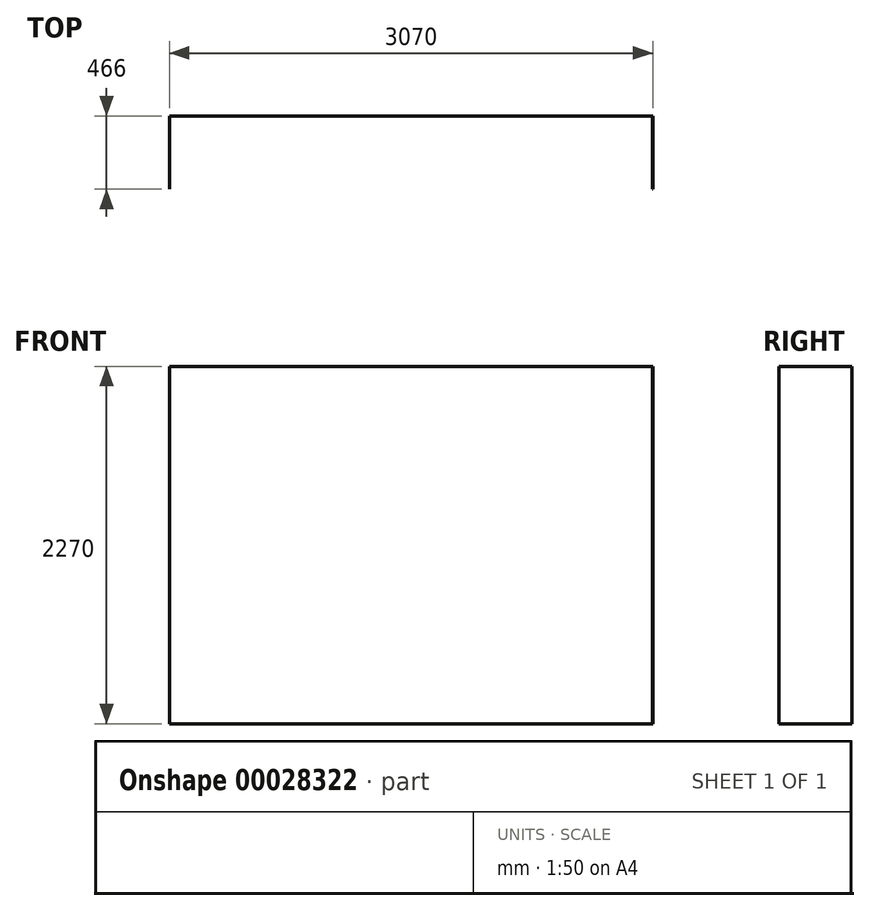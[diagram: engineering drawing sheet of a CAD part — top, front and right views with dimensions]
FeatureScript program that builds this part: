
annotation { "Feature Type Name" : "Feature", "Feature Type Description" : "" }
export const myFeature = defineFeature(function(context is Context, id is Id, definition is map)
    precondition{}
    {
        {
            var Q0;
            Q0=qCreatedBy(makeId("Front.planeOp"),FACE);
            var sketch = newSketch(context, id + "F0", { "sketchPlane" : qUnion([Q0])});
            skLineSegment(sketch, "E0.bottom", {"start": v(-1527.48, 1543.98) * mm, "end": v(1542.52, 1543.98) * mm});
            skLineSegment(sketch, "E0.top", {"start": v(-1527.48, -726.02) * mm, "end": v(1542.52, -726.02) * mm});
            skLineSegment(sketch, "E0.left", {"start": v(-1527.48, 1543.98) * mm, "end": v(-1527.48, -726.02) * mm});
            skLineSegment(sketch, "E0.right", {"start": v(1542.52, 1543.98) * mm, "end": v(1542.52, -726.02) * mm});
            skSolve(sketch);
        }
        {
            var Q0;
            Q0 = qSketchRegion(id + "F0", true);
            extrude(context, id + "F1", {"entities" : qUnion([Q0]), "oppositeDirection" : true, "depth" : 1 * mm});
        }
        {
            var Q0;
            Q0=makeQuery(id+"F1.opExtrude","CAP_FACE",FACE,{"disambiguationData":[OSD([sQuery(id+"F0.wireOp",EDGE,"E0.bottom"),sQuery(id+"F0.wireOp",EDGE,"E0.top"),sQuery(id+"F0.wireOp",EDGE,"E0.left"),sQuery(id+"F0.wireOp",EDGE,"E0.right")])],"isStart":true});
            var sketch = newSketch(context, id + "F2", { "sketchPlane" : qUnion([Q0])});
            skLineSegment(sketch, "E1.bottom", {"start": v(-1527.48, 1543.98) * mm, "end": v(-1526.48, 1543.98) * mm});
            skLineSegment(sketch, "E1.top", {"start": v(-1527.48, -726.02) * mm, "end": v(-1526.48, -726.02) * mm});
            skLineSegment(sketch, "E1.left", {"start": v(-1527.48, 1543.98) * mm, "end": v(-1527.48, -726.02) * mm});
            skLineSegment(sketch, "E1.right", {"start": v(-1526.48, 1543.98) * mm, "end": v(-1526.48, -726.02) * mm});
            skLineSegment(sketch, "E2.bottom", {"start": v(1542.52, 1543.98) * mm, "end": v(1541.52, 1543.98) * mm});
            skLineSegment(sketch, "E2.top", {"start": v(1542.52, -726.02) * mm, "end": v(1541.52, -726.02) * mm});
            skLineSegment(sketch, "E2.left", {"start": v(1542.52, 1543.98) * mm, "end": v(1542.52, -726.02) * mm});
            skLineSegment(sketch, "E2.right", {"start": v(1541.52, 1543.98) * mm, "end": v(1541.52, -726.02) * mm});
            skSolve(sketch);
        }
        {
            var Q0;
            Q0 = qSketchRegion(id + "F2", true);
            extrude(context, id + "F3", {"entities" : qUnion([Q0]), "operationType" : NewBodyOperationType.ADD, "depth" : 465 * mm});
        }
    });
